# Revit family: NBS_DudleyIndustriesLimited_PprTwlDpnsrs_Dementia_MultifoldPaperTowelDispenser
name_source: partatom
category: Specialty Equipment
revit_build: Autodesk Revit 2017 (Build: 20171027_0315(x64)
units: mm (PartAtom-declared; Revit-internal decimal feet)

## family parameters
Cut with Voids When Loaded = No
Host = Face
Part Type = Normal
Room Calculation Point = No
Round Connector Dimension = Use Diameter
Shared = No

## types (1)
- Dementia_MultifoldPaperTowelDispenser
    AssetType = Fixed
    BIMObjectName = NBS_DudleyIndustriesLimited_PaperTowelDispensers_Dementia_MultifoldPaperTowelDispenser
    Category = Pr_40_70_22_62:Paper towel dispensers
    Color = White, Blue
    Default Elevation = 1200 mm
    Description = Multi-fold paper towel dispenser
    DurationUnit = year
    Features = No sharp edges or corners, robust and durable, works in conjunction with the Wall Plates 78832BL (blue) and 78832WH (white) to provide an anti-ligature solution for high risk areas
    Finish = Powder coated
    Form = Wall mounted
    IfcExportAs = IfcSanitaryTerminalType
    IfcExportType = UNDEFINED
    IntegralAccessories = Wall plate
    ManufacturerName = Dudley Industries Limited
    ManufacturerURL = https://www.dudleyindustries.com
    Material = Stainless steel
    MaterialsBody = Stainless steel
    ModelNumber = 78830WH (white), 78830BL (blue)
    ModelReference = Dementia Multi-fold Paper Towel Dispenser
    NBSCertification = www.nationalbimlibrary.com/cert/flbnwwlu
    NBSDescription = Paper towel dispensers
    NBSReference = 45-35-72/344
    Name = PaperTowelDispensers_Dementia:Multi-foldPaperTowelDispenser_DudleyIndustriesLimited
    NominalDepth = 127 mm
    NominalHeight = 250 mm
    NominalLength = 0 mm  [stored 0 ft]
    NominalWidth = 336 mm  [stored 1.10236 ft]
    Operation = Pull out dispenser
    PackingCarton = 1 piece
    ProductInformation = https://dudleyindustries.com
    Shape = Square
    Size = 259 x 250 x 126 mm
    Status = UNSET
    TowelDispenserCasingMaterial = NBS_Concept
    Uniclass2015Code = Pr_40_70_22_62
    Uniclass2015Title = Paper towel dispensers
    Uniclass2015Version = Products v1.11
    Version = 1
    WallPlateMaterial = NBS_Concept
    WarrantyDurationUnit = year

note: [stored X ft] marks values corroborated as IEEE doubles in the binary element streams (Revit-internal decimal feet)

## geometry (parser evidence)
native form markers: Sweep x2
no freeform markers — native parametric forms only
